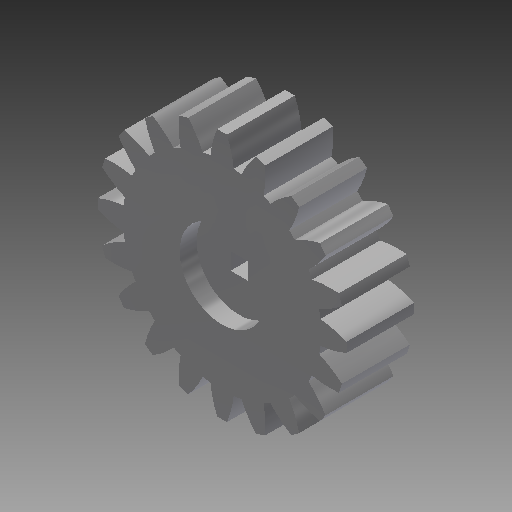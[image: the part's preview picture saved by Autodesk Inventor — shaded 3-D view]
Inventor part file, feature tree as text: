
AUTODESK INVENTOR PART (.ipt)
format: ipt  version: 2019 (Build 230136000, 136)  size: 291,328 bytes
history: native  units: mm (DEFAULTED — no unit token found)
features: sketch x4, extrude x3, plane x3, other x3
ambient origin geometry x8: Origin, YZ Plane, XZ Plane, XY Plane, X Axis, Y Axis, Z Axis, Center Point
bodies: Solid1 (feature_tree)
feature tree (13):
  extrude  "Extrusion1"  Depth=12.0mm TaperAngle=0.0deg
  plane  "Work Plane2"
  plane  "Work Plane8"
  plane  "Work Plane9"
  other  "Spur Gear"
  extrude  "Extrusion2"  Depth=10.0mm TaperAngle=0.0deg
  extrude  "Extrusion3"  Depth=1.570796mm TaperAngle=0.0deg
  sketch  "Sketch1"  dims[d0=44.0mm d1=12.0mm d2=0.0mm]
  sketch  "Sketch2"  dims[d3=40.0mm d4=10.0mm d5=0.0mm]
  other  "Srf1"
  sketch  "Sketch5"  dims[d16=40.0mm d17=0.0mm d34=1.570796mm]
  sketch  "Sketch6"  dims[d39=0.0mm d41=0.0mm d43=40.0mm d46=40.0mm d47=0.0mm d48=0.0mm d49=3.0mm d50=3.0mm d51=12.0mm d52=0.0mm d53=15.0mm d54=3.0mm d55=0.0mm]
  other  "Pitch Diameter"
